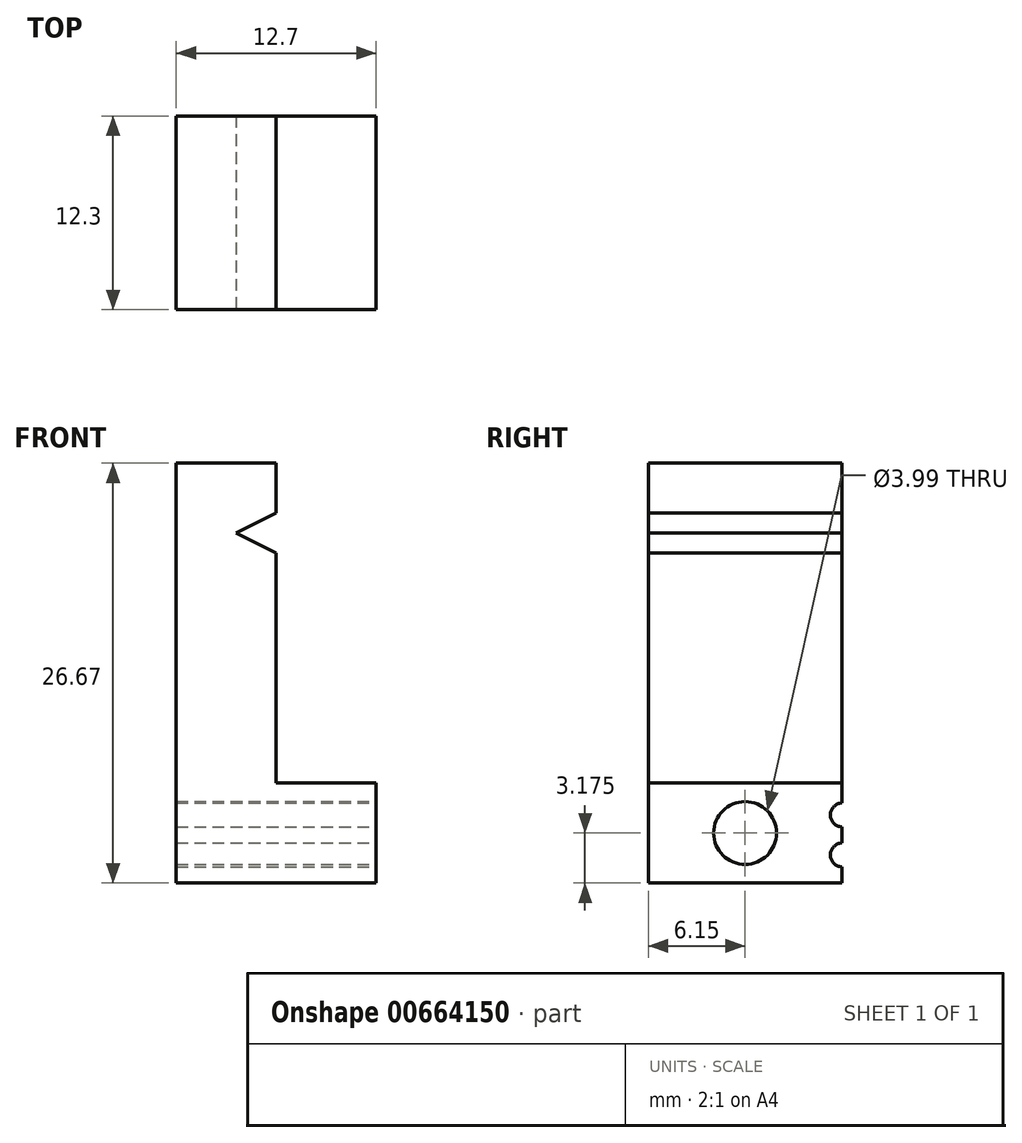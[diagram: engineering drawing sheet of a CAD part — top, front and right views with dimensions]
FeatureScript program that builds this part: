
annotation { "Feature Type Name" : "Feature", "Feature Type Description" : "" }
export const myFeature = defineFeature(function(context is Context, id is Id, definition is map)
    precondition{}
    {
        {
            var Q0;
            Q0=qCreatedBy(makeId("Top.planeOp"),FACE);
            var sketch = newSketch(context, id + "F0", { "sketchPlane" : qUnion([Q0])});
            skLineSegment(sketch, "E0.bottom", {"start": v(-6.35, 6.15) * mm, "end": v(6.35, 6.15) * mm});
            skLineSegment(sketch, "E0.top", {"start": v(-6.35, -6.15) * mm, "end": v(6.35, -6.15) * mm});
            skLineSegment(sketch, "E0.left", {"start": v(-6.35, 6.15) * mm, "end": v(-6.35, -6.15) * mm});
            skLineSegment(sketch, "E0.right", {"start": v(6.35, 6.15) * mm, "end": v(6.35, -6.15) * mm});
            skPoint(sketch, "E0.middle", {"position": v(0, 0) * mm});
            skSolve(sketch);
        }
        {
            var Q0;
            Q0=makeQuery(id+"F0.imprint","IMPRINT",FACE,{"disambiguationData":[TD([[makeQuery(id+"F0.imprint","IMPRINT",EDGE,{"derivedFrom":sQuery(id+"F0.wireOp",EDGE,"E0.bottom")}),-1.0]])]});
            extrude(context, id + "F1", {"entities" : qUnion([Q0]), "depth" : 6.35 * mm, "offsetDistance" : 25.4 * mm});
        }
        {
            var Q0;
            Q0=makeQuery(id+"F1.opExtrude","CAP_FACE",FACE,{"disambiguationData":[OSD([sQuery(id+"F0.wireOp",EDGE,"E0.bottom"),sQuery(id+"F0.wireOp",EDGE,"E0.top"),sQuery(id+"F0.wireOp",EDGE,"E0.left"),sQuery(id+"F0.wireOp",EDGE,"E0.right")])],"isStart":false});
            var sketch = newSketch(context, id + "F2", { "sketchPlane" : qUnion([Q0])});
            skLineSegment(sketch, "E1.bottom", {"start": v(-6.35, 6.15) * mm, "end": v(0, 6.15) * mm});
            skLineSegment(sketch, "E1.top", {"start": v(-6.35, -6.15) * mm, "end": v(0, -6.15) * mm});
            skLineSegment(sketch, "E1.left", {"start": v(-6.35, 6.15) * mm, "end": v(-6.35, -6.15) * mm});
            skLineSegment(sketch, "E1.right", {"start": v(0, 6.15) * mm, "end": v(0, -6.15) * mm});
            skSolve(sketch);
        }
        {
            var Q0;
            Q0=makeQuery(id+"F2.imprint","IMPRINT",FACE,{"disambiguationData":[TD([[makeQuery(id+"F2.imprint","IMPRINT",EDGE,{"derivedFrom":sQuery(id+"F2.wireOp",EDGE,"E1.bottom")}),-1.0]])]});
            extrude(context, id + "F3", {"entities" : qUnion([Q0]), "operationType" : NewBodyOperationType.ADD, "depth" : 20.32 * mm, "offsetDistance" : 25.4 * mm});
        }
        {
            var Q0;
            Q0=makeQuery(id+"F1.opExtrude","SWEPT_FACE",FACE,{"disambiguationData":[OSD([sQuery(id+"F0.wireOp",EDGE,"E0.right")])]});
            var sketch = newSketch(context, id + "F4", { "sketchPlane" : qUnion([Q0])});
            skCircle(sketch, "E2", {"center": v(0, 3.18) * mm, "radius": 2 * mm});
            skPoint(sketch, "E2.centerSnap0", {"position": v(-6.15, 3.18) * mm});
            skSolve(sketch);
        }
        {
            var Q0;
            Q0=makeQuery(id+"F4.imprint","IMPRINT",FACE,{"disambiguationData":[TD([[makeQuery(id+"F4.imprint","IMPRINT",EDGE,{"derivedFrom":sQuery(id+"F4.wireOp",EDGE,"E2")}),1.0]])]});
            extrude(context, id + "F5", {"entities" : qUnion([Q0]), "operationType" : NewBodyOperationType.REMOVE, "endBound" : BoundingType.THROUGH_ALL, "oppositeDirection" : true, "depth" : 25.4 * mm, "offsetDistance" : 25.4 * mm});
        }
        {
            var Q0;
            Q0=makeQuery(id+"F3.boolean.opBoolean","MERGE",FACE,{"derivedFrom":[makeQuery(id+"F1.opExtrude","SWEPT_FACE",FACE,{"disambiguationData":[OSD([sQuery(id+"F0.wireOp",EDGE,"E0.top")])]}),makeQuery(id+"F3.opExtrude","SWEPT_FACE",FACE,{"disambiguationData":[OSD([sQuery(id+"F2.wireOp",EDGE,"E1.top")])]})]});
            var sketch = newSketch(context, id + "F6", { "sketchPlane" : qUnion([Q0])});
            skLineSegment(sketch, "E3.left", {"start": v(0, 23.5) * mm, "end": v(0, 20.96) * mm});
            skLineSegment(sketch, "E4", {"start": v(-2.54, 22.23) * mm, "end": v(0, 23.5) * mm});
            skLineSegment(sketch, "E5", {"start": v(-2.54, 22.23) * mm, "end": v(0, 20.96) * mm});
            skSolve(sketch);
        }
        {
            var Q0;
            Q0=makeQuery(id+"F6.imprint","IMPRINT",FACE,{"disambiguationData":[TD([[makeQuery(id+"F6.imprint","IMPRINT",EDGE,{"derivedFrom":sQuery(id+"F6.wireOp",EDGE,"E3.left")}),-1.0]])]});
            extrude(context, id + "F7", {"entities" : qUnion([Q0]), "operationType" : NewBodyOperationType.REMOVE, "endBound" : BoundingType.THROUGH_ALL, "oppositeDirection" : true, "depth" : 25.4 * mm, "offsetDistance" : 25.4 * mm});
        }
        {
            var Q0;
            Q0=makeQuery(id+"F1.opExtrude","SWEPT_FACE",FACE,{"disambiguationData":[OSD([sQuery(id+"F0.wireOp",EDGE,"E0.right")])]});
            var sketch = newSketch(context, id + "F8", { "sketchPlane" : qUnion([Q0])});
            skLineSegment(sketch, "E6.left", {"start": v(-6.15, 1.02) * mm, "end": v(-6.21, 2.54) * mm});
            skLineSegment(sketch, "E7.left", {"start": v(-6.15, 3.56) * mm, "end": v(-6.21, 5.08) * mm});
            skLineSegment(sketch, "E8.MirrorCS", {"start": v(6.15, 1.02) * mm, "end": v(6.21, 2.54) * mm});
            skLineSegment(sketch, "E9.MirrorCS", {"start": v(6.15, 3.56) * mm, "end": v(6.21, 5.08) * mm});
            skArc(sketch, "E10", {"start": v(-6.21, 5.08) * mm, "mid": v(-5.42, 4.35) * mm, "end": v(-6.15, 3.56) * mm});
            skArc(sketch, "E11", {"start": v(-6.21, 2.54) * mm, "mid": v(-5.42, 1.81) * mm, "end": v(-6.15, 1.02) * mm});
            skArc(sketch, "E12.MirrorCS", {"start": v(6.21, 5.08) * mm, "mid": v(5.42, 4.35) * mm, "end": v(6.15, 3.56) * mm});
            skArc(sketch, "E13.MirrorCS", {"start": v(6.21, 2.54) * mm, "mid": v(5.42, 1.81) * mm, "end": v(6.15, 1.02) * mm});
            skSolve(sketch);
        }
        {
            var Q0;
            {var subQ0=sQuery(id+"F8.wireOp",EDGE,"E10");var subQ1=makeQuery(id+"F1.opExtrude","SWEPT_EDGE",EDGE,{"disambiguationData":[OSD([sQuery(id+"F0.wireOp",EDGE,"E0.top"),sQuery(id+"F0.wireOp",EDGE,"E0.right")])]});var subQ3=makeQuery(id+"F8.imprint","INTERSECT",VERTEX,{"derivedFrom":[subQ1,subQ0]});Q0=makeQuery(id+"F8.imprint","IMPRINT",FACE,{"disambiguationData":[TD([[makeQuery(id+"F8.imprint","IMPRINT",EDGE,{"disambiguationData":[TD([[subQ3,-1.0]])],"derivedFrom":subQ0}),-1.0]])]});}
            var Q1;
            {var subQ0=sQuery(id+"F8.wireOp",EDGE,"E11");var subQ1=makeQuery(id+"F1.opExtrude","SWEPT_EDGE",EDGE,{"disambiguationData":[OSD([sQuery(id+"F0.wireOp",EDGE,"E0.top"),sQuery(id+"F0.wireOp",EDGE,"E0.right")])]});var subQ3=makeQuery(id+"F8.imprint","INTERSECT",VERTEX,{"derivedFrom":[subQ1,subQ0]});Q1=makeQuery(id+"F8.imprint","IMPRINT",FACE,{"disambiguationData":[TD([[makeQuery(id+"F8.imprint","IMPRINT",EDGE,{"disambiguationData":[TD([[subQ3,-1.0]])],"derivedFrom":subQ0}),-1.0]])]});}
            var Q2;
            {var subQ0=sQuery(id+"F8.wireOp",EDGE,"E13.MirrorCS");var subQ1=makeQuery(id+"F1.opExtrude","SWEPT_EDGE",EDGE,{"disambiguationData":[OSD([sQuery(id+"F0.wireOp",EDGE,"E0.bottom"),sQuery(id+"F0.wireOp",EDGE,"E0.right")])]});var subQ3=makeQuery(id+"F8.imprint","INTERSECT",VERTEX,{"derivedFrom":[subQ1,subQ0]});Q2=makeQuery(id+"F8.imprint","IMPRINT",FACE,{"disambiguationData":[TD([[makeQuery(id+"F8.imprint","IMPRINT",EDGE,{"disambiguationData":[TD([[subQ3,-1.0]])],"derivedFrom":subQ0}),1.0]])]});}
            var Q3;
            {var subQ0=sQuery(id+"F8.wireOp",EDGE,"E12.MirrorCS");var subQ1=makeQuery(id+"F1.opExtrude","SWEPT_EDGE",EDGE,{"disambiguationData":[OSD([sQuery(id+"F0.wireOp",EDGE,"E0.bottom"),sQuery(id+"F0.wireOp",EDGE,"E0.right")])]});var subQ3=makeQuery(id+"F8.imprint","INTERSECT",VERTEX,{"derivedFrom":[subQ1,subQ0]});Q3=makeQuery(id+"F8.imprint","IMPRINT",FACE,{"disambiguationData":[TD([[makeQuery(id+"F8.imprint","IMPRINT",EDGE,{"disambiguationData":[TD([[subQ3,-1.0]])],"derivedFrom":subQ0}),1.0]])]});}
            extrude(context, id + "F9", {"entities" : qUnion([Q0, Q1, Q2, Q3]), "operationType" : NewBodyOperationType.REMOVE, "endBound" : BoundingType.THROUGH_ALL, "oppositeDirection" : true, "depth" : 25.4 * mm, "offsetDistance" : 25.4 * mm});
        }
    });
